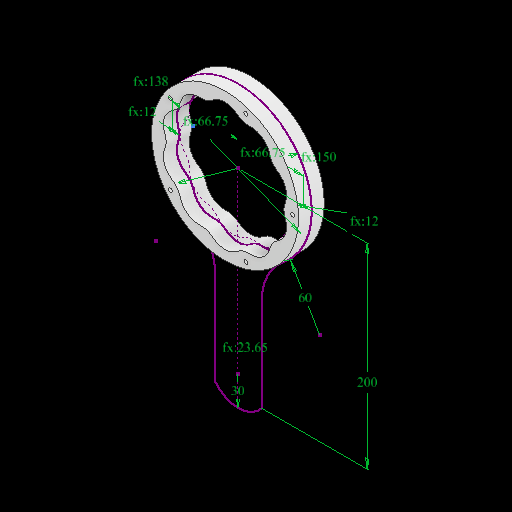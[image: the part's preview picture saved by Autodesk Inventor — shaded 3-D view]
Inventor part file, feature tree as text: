
AUTODESK INVENTOR PART (.ipt)
format: ipt  version: 2022.2 (Build 262287010, 287A)  size: 307,200 bytes
history: native  units: mm
features: sketch x11, extrude x8, pattern_circular x3, other x2, plane x1, hole x1, fillet x1
ambient origin geometry x8: Origin, YZ Plane, XZ Plane, XY Plane, X Axis, Y Axis, Z Axis, Center Point
bodies: Solid3 (feature_tree)
feature tree (27):
  sketch  "Sketch3"  dims[d59=66.75mm d61=0.0mm d62=3600.0mm]
  sketch  "Sketch1"  dims[d4=150.0mm d19=12.0mm]
  plane  "Work Plane1"
  sketch  "Sketch9"  dims[d94=30.0mm d95=200.0mm]
  extrude  "Extrusion7"  Depth=12.0mm
  sketch  "Sketch10"  dims[d96=23.65mm d97=26.0mm d98=0.0mm]
  extrude  "Extrusion10"  Depth=3600.0mm TaperAngle=0.0deg
  pattern_circular  "Circular Pattern4"  Count=6  [1 undecoded]
  extrude  "Extrusion8"  Depth=200.0mm
  extrude  "Extrusion9"  Depth=26.0mm TaperAngle=0.0deg
  pattern_circular  "Circular Pattern3"  [2 undecoded]
  extrude  "Extrusion3"  Depth=2.0mm TaperAngle=0.0deg
  hole  "Hole3"  [1 undecoded]
  pattern_circular  "Circular Pattern5"  [2 undecoded]
  sketch  "Sketch4"  dims[d66=12.0mm]
  sketch  "Sketch5"  dims[d67=66.75mm]
  sketch  "Sketch6"  dims[d68=138.0mm]
  extrude  "Extrusion4"  Depth=2.0mm TaperAngle=0.0deg
  sketch  "Sketch7"  dims[d69=26.3mm d70=0.0mm]
  extrude  "Extrusion6"  Depth=2.0mm
  fillet  "Fillet1"  [1 undecoded]
  extrude  "Extrusion11"  Depth=2.0mm
  other  "2D Equation Curve10"
  sketch  "Sketch8"  dims[d91=23.65mm d93=60.0mm]
  other  "2D Equation Curve11"
  sketch  "Sketch11"  dims[d99=156.0mm]
  sketch  "Sketch12"  dims[d102=29.0mm d103=0.0mm d104=2.0mm d105=0.0mm d106=3600.0mm d111=100.0mm d112=69.0mm d113=2.5mm d114=0.0mm d115=3.0mm d116=0.0mm d117=0.0mm d118=5.5mm d119=2.5mm d120=0.0mm d121=50.0mm d122=360.0deg d124=2.5mm d125=0.0mm d126=50.0mm d127=360.0deg d129=22.5mm d130=2.5mm d131=0.0mm d132=138.0mm d133=4.0mm d134=6.0mm d135=4.0mm d136=2.0mm d137=90.0deg d138=4.0mm d139=0.0mm d140=50.0mm d141=360.0deg]
note: 7 required parameter values undecoded (feature->parameter linkage not recoverable at this tier; creation-order binding heuristic only, values carry confidence <= 0.55)
